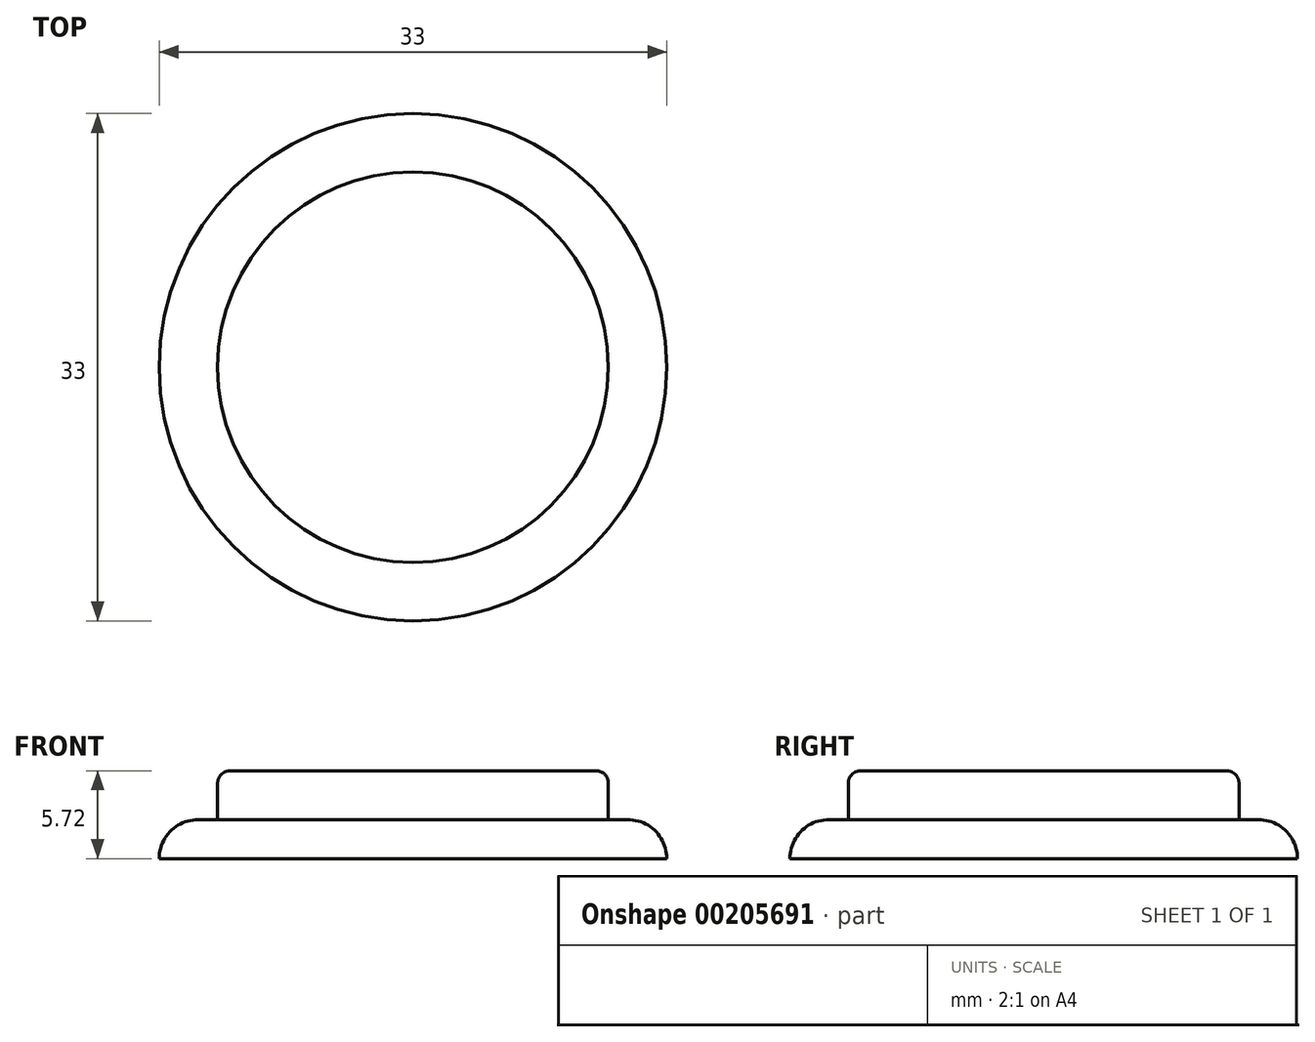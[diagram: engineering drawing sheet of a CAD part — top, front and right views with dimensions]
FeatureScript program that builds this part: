
annotation { "Feature Type Name" : "Feature", "Feature Type Description" : "" }
export const myFeature = defineFeature(function(context is Context, id is Id, definition is map)
    precondition{}
    {
        {
            var Q0;
            Q0=qCreatedBy(makeId("Top.planeOp"),FACE);
            var sketch = newSketch(context, id + "F0", { "sketchPlane" : qUnion([Q0])});
            skCircle(sketch, "E0", {"center": v(0, 0) * mm, "radius": 16.5 * mm});
            skSolve(sketch);
        }
        {
            var Q0;
            Q0=makeQuery(id+"F0.imprint","IMPRINT",FACE,{"disambiguationData":[TD([[makeQuery(id+"F0.imprint","IMPRINT",EDGE,{"derivedFrom":sQuery(id+"F0.wireOp",EDGE,"E0")}),1.0]])]});
            extrude(context, id + "F1", {"entities" : qUnion([Q0]), "depth" : 2.54 * mm});
        }
        {
            var Q0;
            Q0=makeQuery(id+"F1.opExtrude","CAP_FACE",FACE,{"disambiguationData":[OSD([sQuery(id+"F0.wireOp",EDGE,"E0")])],"isStart":false});
            var sketch = newSketch(context, id + "F2", { "sketchPlane" : qUnion([Q0])});
            skCircle(sketch, "E1", {"center": v(0, 0) * mm, "radius": 12.7 * mm});
            skSolve(sketch);
        }
        {
            var Q0;
            Q0=makeQuery(id+"F2.imprint","IMPRINT",FACE,{"disambiguationData":[TD([[makeQuery(id+"F2.imprint","IMPRINT",EDGE,{"derivedFrom":sQuery(id+"F2.wireOp",EDGE,"E1")}),1.0]])]});
            extrude(context, id + "F3", {"entities" : qUnion([Q0]), "operationType" : NewBodyOperationType.ADD, "depth" : 3.17 * mm});
        }
        {
            var Q0;
            Q0=makeQuery(id+"F1.opExtrude","CAP_EDGE",EDGE,{"disambiguationData":[OSD([sQuery(id+"F0.wireOp",EDGE,"E0")])],"isStart":false});
            fillet(context, id + "F4", {"entities" : qUnion([Q0]), "radius" : 2.54 * mm, "tangentPropagation" : true, "allowEdgeOverflow" : false});
        }
        {
            var Q0;
            Q0=makeQuery(id+"F3.opExtrude","CAP_EDGE",EDGE,{"disambiguationData":[OSD([sQuery(id+"F2.wireOp",EDGE,"E1")])],"isStart":false});
            fillet(context, id + "F5", {"entities" : qUnion([Q0]), "radius" : 0.8 * mm, "tangentPropagation" : true, "allowEdgeOverflow" : false});
        }
    });
